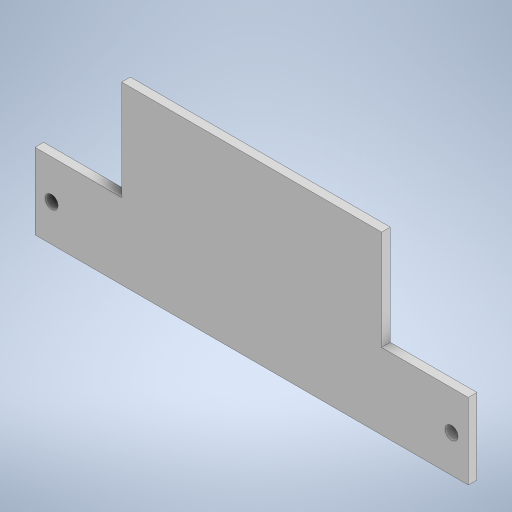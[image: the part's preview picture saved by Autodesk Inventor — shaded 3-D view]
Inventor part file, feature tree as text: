
AUTODESK INVENTOR PART (.ipt)
format: ipt  version: 2023 (Build 270158000, 158)  size: 249,856 bytes
history: native  units: in
note: dims shown in document units (in); Inventor stores cm internally (conversion verified against a paired STEP export)
features: reference x12, other x6, extrude x5, sketch x5, projected_geometry x1
ambient origin geometry x8: Origin, YZ Plane, XZ Plane, XY Plane, X Axis, Y Axis, Z Axis, Center Point
bodies: Body1 (feature_tree)
feature tree (29):
  other  "Bryła1"
  extrude  "Wyciągnięcie proste1"  Depth=0.6496in
  extrude  "Wyciągnięcie proste2"  Depth=0.0787in TaperAngle=0.0deg
  extrude  "Wyciągnięcie proste3"  Depth=0.0787in TaperAngle=0.0deg
  extrude  "Wyciągnięcie proste4"  Depth=0.6693in
  extrude  "Wyciągnięcie proste5"  Depth=0.0787in TaperAngle=0.0deg
  sketch  "Szkic1"
  reference  "Odniesienie1"
  reference  "Odniesienie2"
  reference  "Odniesienie3"
  reference  "Odniesienie4"
  reference  "Odniesienie5"
  reference  "Odniesienie6"
  reference  "Odniesienie7"
  reference  "Odniesienie8"
  reference  "Odniesienie9"
  reference  "Odniesienie10"
  sketch  "Szkic2"
  reference  "Odniesienie11"
  sketch  "Szkic3"
  projected_geometry  "Pętla rzutowana1"
  sketch  "Szkic4"
  reference  "Odniesienie12"
  sketch  "Szkic5"
  other  "<userpath>\Desktop\MojeRoboty\Stefan\mechanics 2\STEFAN.iam"
  other  "STEFAN.iam"
  other  "sciana_awaryjna:1"
  other  "dach:1"
  other  "uchwyt_silnikow:1"
